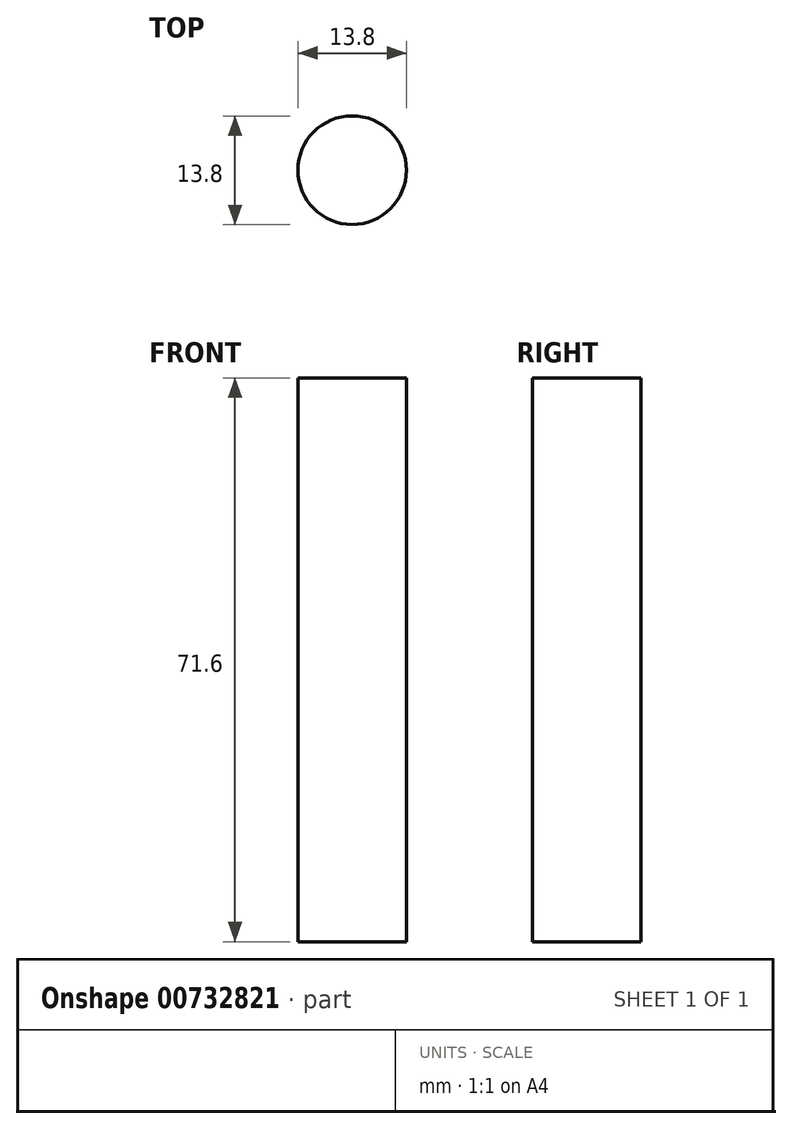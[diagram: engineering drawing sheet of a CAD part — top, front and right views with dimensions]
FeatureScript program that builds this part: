
annotation { "Feature Type Name" : "Feature", "Feature Type Description" : "" }
export const myFeature = defineFeature(function(context is Context, id is Id, definition is map)
    precondition{}
    {
        {
            var Q0;
            Q0=qCreatedBy(makeId("Front.planeOp"),FACE);
            var sketch = newSketch(context, id + "F0", { "sketchPlane" : qUnion([Q0])});
            skLineSegment(sketch, "E0", {"start": v(0, 71.6) * mm, "end": v(0, 0) * mm});
            skLineSegment(sketch, "E1", {"start": v(0, 0) * mm, "end": v(-6.9, 0) * mm});
            skLineSegment(sketch, "E2", {"start": v(-6.9, 0) * mm, "end": v(-6.9, 71.6) * mm});
            skLineSegment(sketch, "E3", {"start": v(-6.9, 71.6) * mm, "end": v(0, 71.6) * mm});
            skLineSegment(sketch, "E4", {"start": v(-6.9, 0) * mm, "end": v(-18.5, 0) * mm});
            skLineSegment(sketch, "E5", {"start": v(-18.5, 0) * mm, "end": v(-6.9, 18.34) * mm});
            skLineSegment(sketch, "E6", {"start": v(-6.9, 18.34) * mm, "end": v(-6.9, 0) * mm});
            skSolve(sketch);
        }
        {
            var Q0;
            Q0=makeQuery(id+"F0.imprint","IMPRINT",FACE,{"disambiguationData":[TD([[makeQuery(id+"F0.imprint","IMPRINT",EDGE,{"derivedFrom":sQuery(id+"F0.wireOp",EDGE,"E0")}),-1.0]])]});
            var Q1;
            Q1=sQuery(id+"F0.wireOp",EDGE,"E0");
            revolve(context, id + "F1", {"surfaceOperationType" : NewSurfaceOperationType.NEW, "entities" : qUnion([Q0]), "axis" : qUnion([Q1]), "revolveType" : RevolveType.FULL});
        }
    });
